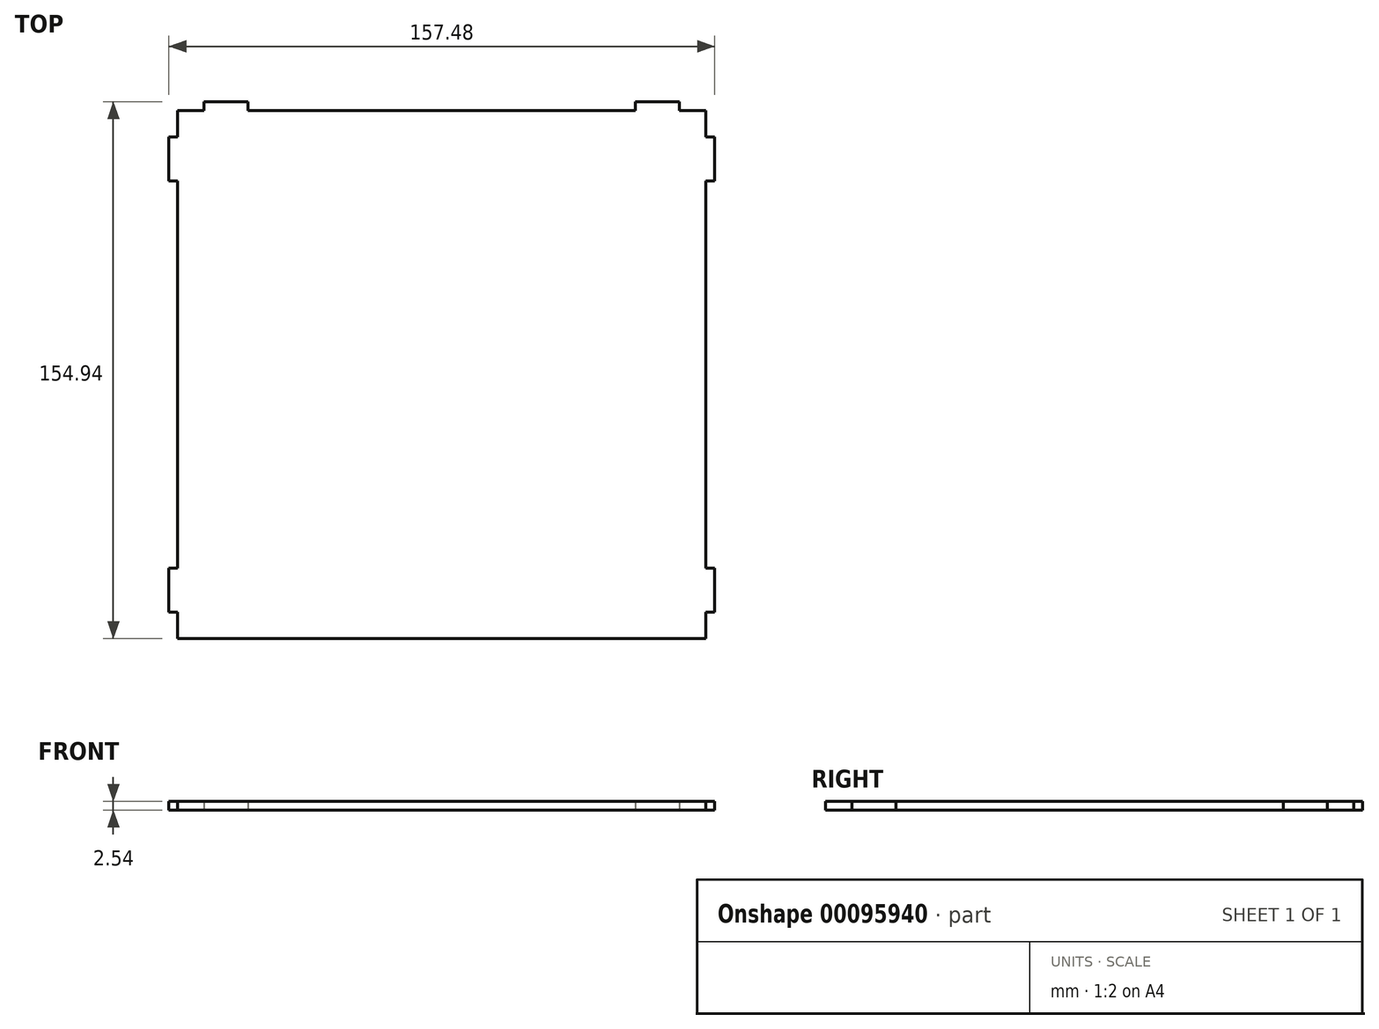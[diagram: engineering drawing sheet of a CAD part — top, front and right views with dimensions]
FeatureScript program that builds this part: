
annotation { "Feature Type Name" : "Feature", "Feature Type Description" : "" }
export const myFeature = defineFeature(function(context is Context, id is Id, definition is map)
    precondition{}
    {
        {
            var Q0;
            Q0=qCreatedBy(makeId("Top.planeOp"),FACE);
            var sketch = newSketch(context, id + "F0", { "sketchPlane" : qUnion([Q0])});
            skLineSegment(sketch, "E0.top", {"start": v(76.2, -76.2) * mm, "end": v(-76.2, -76.2) * mm});
            skPoint(sketch, "E0.middle", {"position": v(0, 0) * mm});
            skLineSegment(sketch, "E1.top", {"start": v(-68.58, 78.74) * mm, "end": v(-55.88, 78.74) * mm});
            skLineSegment(sketch, "E1.left", {"start": v(-68.58, 76.2) * mm, "end": v(-68.58, 78.74) * mm});
            skLineSegment(sketch, "E1.right", {"start": v(-55.88, 76.2) * mm, "end": v(-55.88, 78.74) * mm});
            skLineSegment(sketch, "E2.MirrorCS", {"start": v(68.58, 78.74) * mm, "end": v(55.88, 78.74) * mm});
            skLineSegment(sketch, "E3.MirrorCS", {"start": v(55.88, 76.2) * mm, "end": v(55.88, 78.74) * mm});
            skLineSegment(sketch, "E4.MirrorCS", {"start": v(68.58, 76.2) * mm, "end": v(68.58, 78.74) * mm});
            skLineSegment(sketch, "E5", {"start": v(-76.2, 76.2) * mm, "end": v(-68.58, 76.2) * mm});
            skLineSegment(sketch, "E6", {"start": v(-55.88, 76.2) * mm, "end": v(55.88, 76.2) * mm});
            skLineSegment(sketch, "E7", {"start": v(68.58, 76.2) * mm, "end": v(76.2, 76.2) * mm});
            skLineSegment(sketch, "E8", {"start": v(-76.2, 76.2) * mm, "end": v(-76.2, 68.58) * mm});
            skLineSegment(sketch, "E9", {"start": v(-76.2, -50.8) * mm, "end": v(-76.2, 50.8) * mm});
            skLineSegment(sketch, "E10", {"start": v(-76.2, -68.58) * mm, "end": v(-76.2, -76.2) * mm});
            skLineSegment(sketch, "E11", {"start": v(76.2, -76.2) * mm, "end": v(76.2, -68.58) * mm});
            skLineSegment(sketch, "E12", {"start": v(76.2, 76.2) * mm, "end": v(76.2, 68.58) * mm});
            skLineSegment(sketch, "E13", {"start": v(76.2, 50.8) * mm, "end": v(76.2, -50.8) * mm});
            skLineSegment(sketch, "E14", {"start": v(-76.2, 68.58) * mm, "end": v(-78.74, 68.58) * mm});
            skLineSegment(sketch, "E15", {"start": v(-78.74, 68.58) * mm, "end": v(-78.74, 55.88) * mm});
            skLineSegment(sketch, "E16", {"start": v(-78.74, 55.88) * mm, "end": v(-76.2, 55.88) * mm});
            skLineSegment(sketch, "E17", {"start": v(-76.2, 50.8) * mm, "end": v(-76.2, 55.88) * mm});
            skLineSegment(sketch, "E18.MirrorCS", {"start": v(76.2, 68.58) * mm, "end": v(78.74, 68.58) * mm});
            skLineSegment(sketch, "E19.MirrorCS", {"start": v(78.74, 68.58) * mm, "end": v(78.74, 55.88) * mm});
            skLineSegment(sketch, "E20.MirrorCS", {"start": v(78.74, 55.88) * mm, "end": v(76.2, 55.88) * mm});
            skLineSegment(sketch, "E21.MirrorCS", {"start": v(78.74, -55.88) * mm, "end": v(76.2, -55.88) * mm});
            skLineSegment(sketch, "E22.MirrorCS", {"start": v(78.74, -68.58) * mm, "end": v(78.74, -55.88) * mm});
            skLineSegment(sketch, "E23.MirrorCS", {"start": v(76.2, -68.58) * mm, "end": v(78.74, -68.58) * mm});
            skLineSegment(sketch, "E24.MirrorCS", {"start": v(-78.74, -55.88) * mm, "end": v(-76.2, -55.88) * mm});
            skLineSegment(sketch, "E25.MirrorCS", {"start": v(-76.2, -68.58) * mm, "end": v(-78.74, -68.58) * mm});
            skLineSegment(sketch, "E26.MirrorCS", {"start": v(-78.74, -68.58) * mm, "end": v(-78.74, -55.88) * mm});
            skLineSegment(sketch, "E27", {"start": v(-76.2, -55.88) * mm, "end": v(-76.2, -50.8) * mm});
            skLineSegment(sketch, "E28", {"start": v(76.2, -55.88) * mm, "end": v(76.2, -50.8) * mm});
            skLineSegment(sketch, "E29", {"start": v(76.2, 50.8) * mm, "end": v(76.2, 55.88) * mm});
            skSolve(sketch);
        }
        {
            var Q0;
            Q0=makeQuery(id+"F0.imprint","IMPRINT",FACE,{"disambiguationData":[TD([[makeQuery(id+"F0.imprint","IMPRINT",EDGE,{"derivedFrom":sQuery(id+"F0.wireOp",EDGE,"E0.top")}),-1.0]])]});
            extrude(context, id + "F1", {"entities" : qUnion([Q0]), "depth" : 2.54 * mm});
        }
    });
